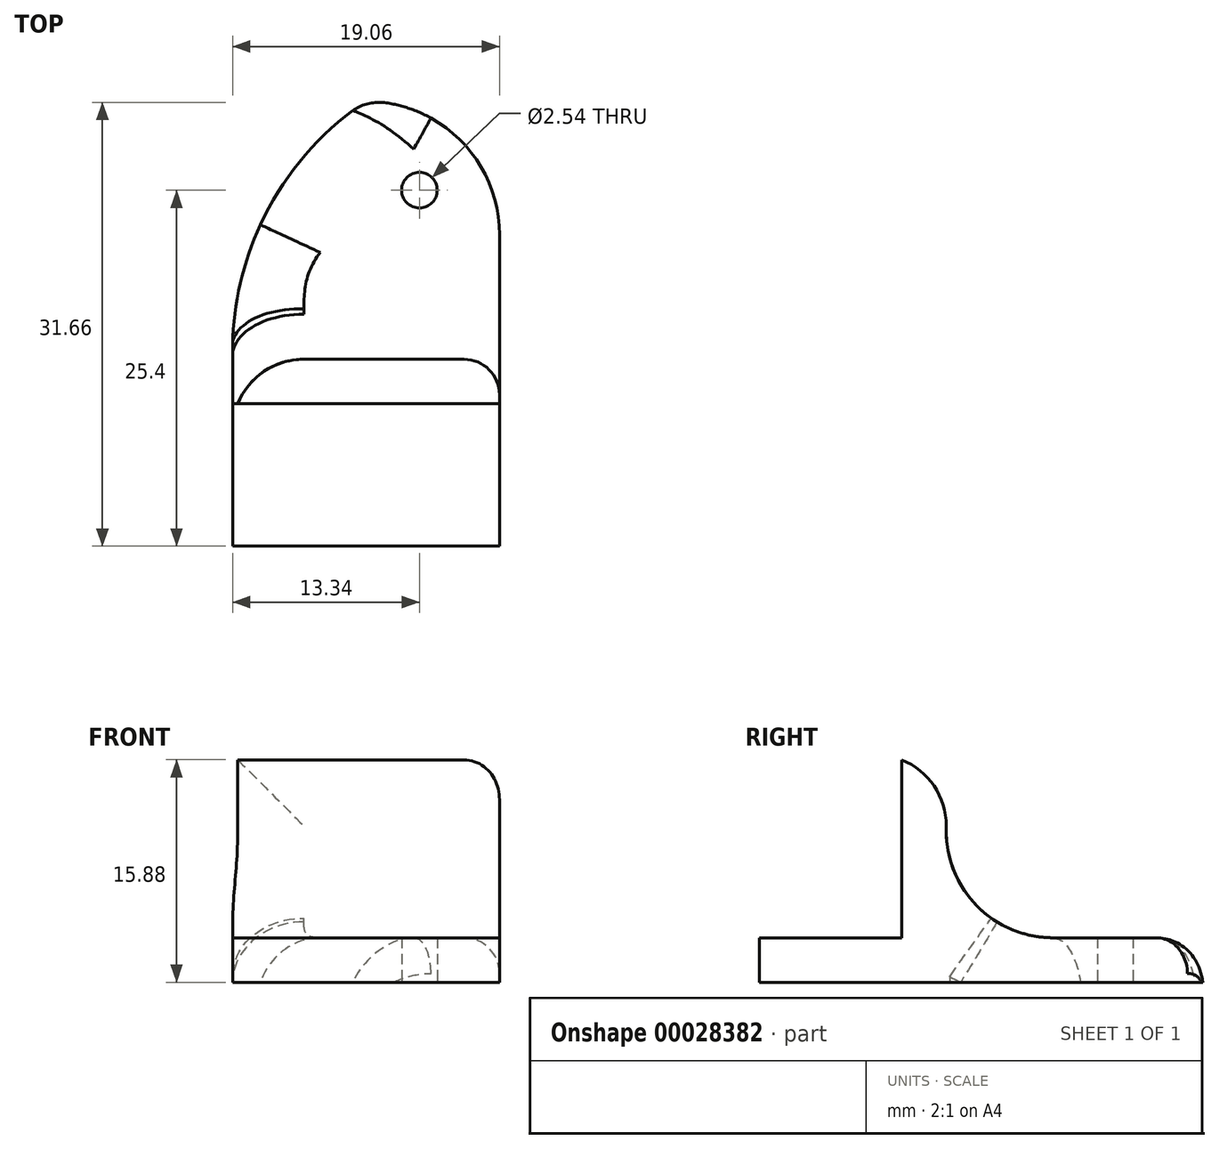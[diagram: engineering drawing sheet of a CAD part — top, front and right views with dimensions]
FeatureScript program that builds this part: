
annotation { "Feature Type Name" : "Feature", "Feature Type Description" : "" }
export const myFeature = defineFeature(function(context is Context, id is Id, definition is map)
    precondition{}
    {
        {
            var Q0;
            Q0=qCreatedBy(makeId("Top.planeOp"),FACE);
            var sketch = newSketch(context, id + "F0", { "sketchPlane" : qUnion([Q0])});
            skLineSegment(sketch, "E0", {"start": v(0, 0) * mm, "end": v(-9.53, 0) * mm});
            skLineSegment(sketch, "E1.MirrorCS", {"start": v(0, 0) * mm, "end": v(9.53, 0) * mm});
            skLineSegment(sketch, "E2.MirrorCS", {"start": v(9.53, 0) * mm, "end": v(9.53, 22.23) * mm});
            skCircle(sketch, "E3", {"center": v(3.81, 25.4) * mm, "radius": 1.27 * mm});
            skArc(sketch, "E4", {"start": v(0, 31.75) * mm, "mid": v(-7.08, 23.88) * mm, "end": v(-9.52, 13.59) * mm});
            skLineSegment(sketch, "E5", {"start": v(-9.53, 13.59) * mm, "end": v(-9.53, 0) * mm});
            skArc(sketch, "E6", {"start": v(9.53, 22.23) * mm, "mid": v(6.74, 28.96) * mm, "end": v(0, 31.75) * mm});
            skSolve(sketch);
        }
        {
            var Q0;
            Q0=qSketchRegion(id+"F0",true);
            extrude(context, id + "F1", {"entities" : qUnion([Q0]), "depth" : 3.17 * mm});
        }
        {
            var Q0;
            Q0=makeQuery(id+"F1.opExtrude","CAP_FACE",FACE,{"disambiguationData":[OSD([sQuery(id+"F0.wireOp",EDGE,"E0"),sQuery(id+"F0.wireOp",EDGE,"6f379fcd-07a3-4692-8b99-ddf4c767372e"),sQuery(id+"F0.wireOp",EDGE,"E1.MirrorCS"),sQuery(id+"F0.wireOp",EDGE,"E2.MirrorCS"),sQuery(id+"F0.wireOp",EDGE,"cfdd0996-df40-48bc-9d6e-5ab92e19fd03"),sQuery(id+"F0.wireOp",EDGE,"bccbf2b4-ea53-4239-b3f4-7ec1dec2db1a")])],"isStart":false});
            var sketch = newSketch(context, id + "F2", { "sketchPlane" : qUnion([Q0])});
            skLineSegment(sketch, "E7.bottom", {"start": v(-9.53, 10.16) * mm, "end": v(9.53, 10.16) * mm});
            skLineSegment(sketch, "E7.top", {"start": v(-9.53, 13.33) * mm, "end": v(9.53, 13.34) * mm});
            skLineSegment(sketch, "E7.left", {"start": v(-9.53, 10.16) * mm, "end": v(-9.53, 13.33) * mm});
            skLineSegment(sketch, "E7.right", {"start": v(9.53, 10.16) * mm, "end": v(9.53, 13.34) * mm});
            skSolve(sketch);
        }
        {
            var Q0;
            Q0=qSketchRegion(id+"F2",true);
            extrude(context, id + "F3", {"entities" : qUnion([Q0]), "operationType" : NewBodyOperationType.ADD, "depth" : 12.7 * mm});
        }
        {
            var Q0;
            Q0=makeQuery(id+"F3.opExtrude","CAP_EDGE",EDGE,{"disambiguationData":[OSD([sQuery(id+"F2.wireOp",EDGE,"E7.top")])],"isStart":true});
            fillet(context, id + "F4", {"entities" : qUnion([Q0]), "radius" : 7.62 * mm, "tangentPropagation" : true, "allowEdgeOverflow" : false});
        }
        {
            var Q0;
            Q0=makeQuery(id+"F4.opFillet","BLEND_EDGE",EDGE,{"blendedFrom":[makeQuery(id+"F3.opExtrude","CAP_EDGE",EDGE,{"disambiguationData":[OSD([sQuery(id+"F2.wireOp",EDGE,"E7.top")])],"isStart":true}),makeQuery(id+"F1.opExtrude","SWEPT_FACE",FACE,{"disambiguationData":[OSD([sQuery(id+"F0.wireOp",EDGE,"E4")])]})],"blendedInto":[makeQuery(id+"F1.opExtrude","SWEPT_FACE",FACE,{"disambiguationData":[OSD([sQuery(id+"F0.wireOp",EDGE,"E4")])]})]});
            var Q1;
            Q1=makeQuery(id+"F3.opExtrude","CAP_EDGE",EDGE,{"disambiguationData":[OSD([sQuery(id+"F2.wireOp",EDGE,"E7.top")])],"isStart":false});
            fillet(context, id + "F5", {"entities" : qUnion([Q0, Q1]), "radius" : 5.08 * mm, "tangentPropagation" : true, "allowEdgeOverflow" : false});
        }
        {
            var Q0;
            Q0=makeQuery(id+"F1.opExtrude","CAP_EDGE",EDGE,{"disambiguationData":[OSD([sQuery(id+"F0.wireOp",EDGE,"E6")])],"isStart":false});
            fillet(context, id + "F6", {"entities" : qUnion([Q0]), "radius" : 2.54 * mm, "tangentPropagation" : true, "allowEdgeOverflow" : false});
        }
    });
